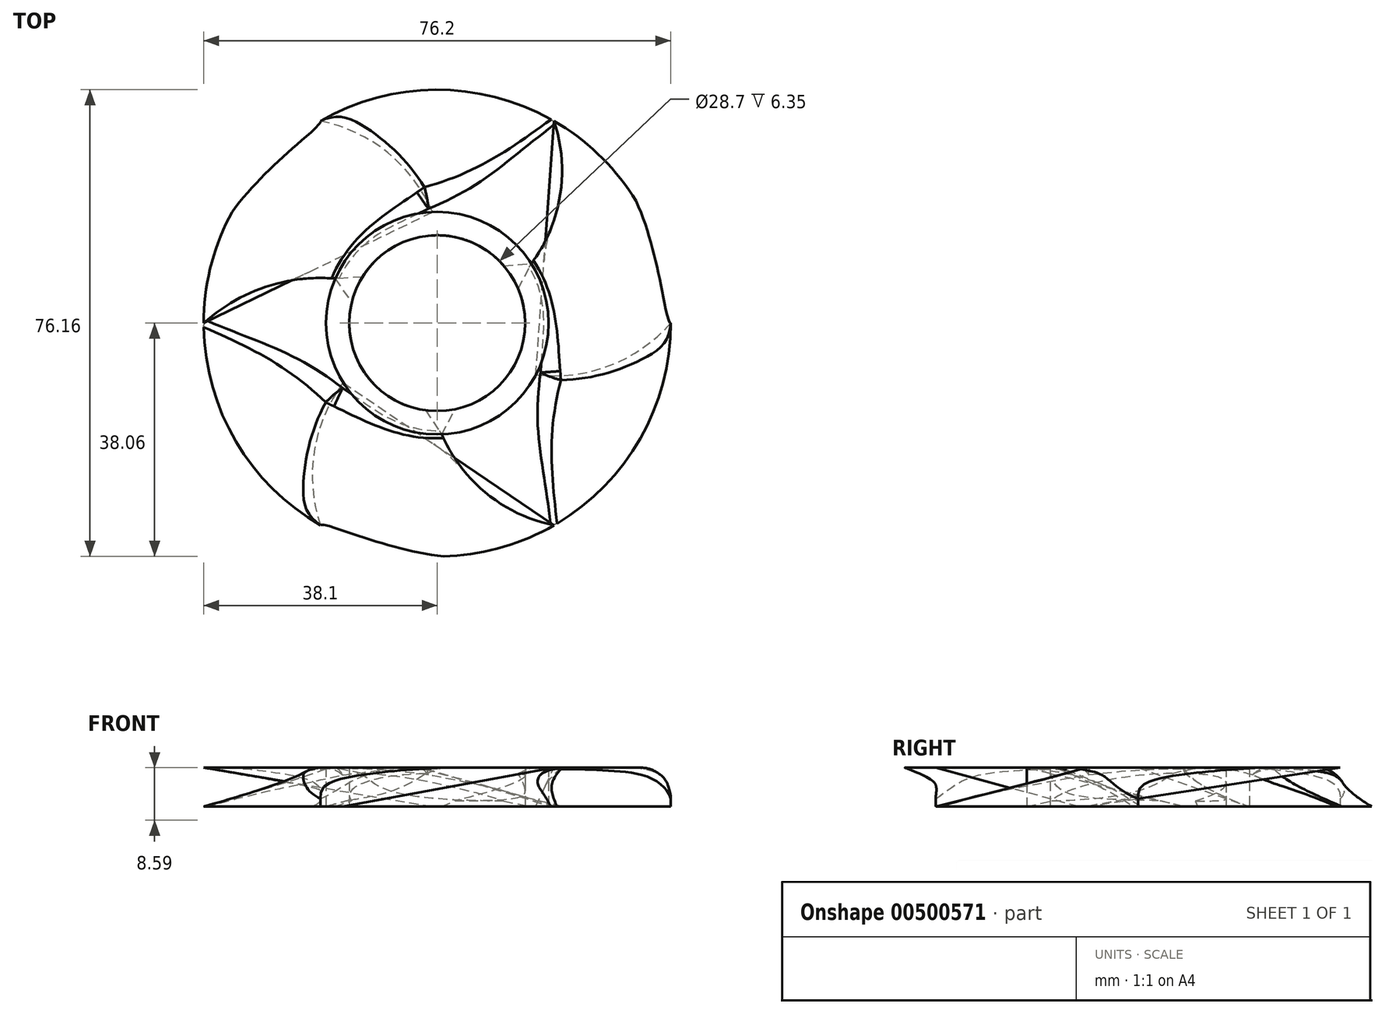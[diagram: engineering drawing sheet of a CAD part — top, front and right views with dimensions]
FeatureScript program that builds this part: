
annotation { "Feature Type Name" : "Feature", "Feature Type Description" : "" }
export const myFeature = defineFeature(function(context is Context, id is Id, definition is map)
    precondition{}
    {
        {
            var Q0;
            Q0=qCreatedBy(makeId("Top.planeOp"),FACE);
            var sketch = newSketch(context, id + "F0", { "sketchPlane" : qUnion([Q0])});
            skCircle(sketch, "E0", {"center": v(0, 0) * mm, "radius": 18.16 * mm});
            skCircle(sketch, "E1.cCircle", {"center": v(0, 0) * mm, "radius": 38.1 * mm, "construction": true});
            skPoint(sketch, "E1.0.midPoint", {"position": v(38.1, 0) * mm});
            skArc(sketch, "E2", {"start": v(15.34, 9.72) * mm, "mid": v(20.06, 20.9) * mm, "end": v(19.05, 33) * mm});
            skArc(sketch, "E3", {"start": v(16.09, -8.43) * mm, "mid": v(28.13, -6.92) * mm, "end": v(38.1, 0) * mm});
            skArc(sketch, "E4", {"start": v(0.75, -18.15) * mm, "mid": v(8.07, -27.82) * mm, "end": v(19.05, -33) * mm});
            skArc(sketch, "E5", {"start": v(-15.34, -9.72) * mm, "mid": v(-20.06, -20.9) * mm, "end": v(-19.05, -33) * mm});
            skArc(sketch, "E6", {"start": v(-16.64, 7.27) * mm, "mid": v(-28.13, 5.88) * mm, "end": v(-38.1, 0) * mm});
            skArc(sketch, "E7", {"start": v(-0.75, 18.15) * mm, "mid": v(-8.07, 27.82) * mm, "end": v(-19.05, 33) * mm});
            skCircle(sketch, "E8", {"center": v(0, 0) * mm, "radius": 38.1 * mm});
            skCircle(sketch, "E9", {"center": v(0, 0) * mm, "radius": 14.35 * mm});
            skSolve(sketch);
        }
        {
            var Q0;
            Q0=qCreatedBy(makeId("Top.planeOp"),FACE);
            cPlane(context, id + "F1", {"entities" : qUnion([Q0]), "cplaneType" : CPlaneType.OFFSET, "offset" : 6.35 * mm, "width" : 152.4 * mm, "height" : 152.4 * mm});
        }
        {
            var Q0;
            Q0=qCreatedBy(id+"F1.planeOp",FACE);
            var sketch = newSketch(context, id + "F2", { "sketchPlane" : qUnion([Q0])});
            skCircle(sketch, "E10", {"center": v(0, 0) * mm, "radius": 18.16 * mm});
            skCircle(sketch, "E11.cCircle", {"center": v(0, 0) * mm, "radius": 38.1 * mm, "construction": true});
            skPoint(sketch, "E11.0.midPoint", {"position": v(38.1, 0) * mm});
            skArc(sketch, "E12", {"start": v(15.34, 9.72) * mm, "mid": v(20.06, 20.9) * mm, "end": v(19.05, 33) * mm});
            skArc(sketch, "E13", {"start": v(16.09, -8.43) * mm, "mid": v(28.13, -6.92) * mm, "end": v(38.1, 0) * mm});
            skArc(sketch, "E14", {"start": v(0.75, -18.15) * mm, "mid": v(8.07, -27.82) * mm, "end": v(19.05, -33) * mm});
            skArc(sketch, "E15", {"start": v(-15.34, -9.72) * mm, "mid": v(-20.06, -20.9) * mm, "end": v(-19.05, -33) * mm});
            skArc(sketch, "E16", {"start": v(-16.64, 7.27) * mm, "mid": v(-28.13, 5.88) * mm, "end": v(-38.1, 0) * mm});
            skArc(sketch, "E17", {"start": v(-0.75, 18.15) * mm, "mid": v(-8.07, 27.82) * mm, "end": v(-19.05, 33) * mm});
            skCircle(sketch, "E18", {"center": v(0, 0) * mm, "radius": 38.1 * mm});
            skCircle(sketch, "E19", {"center": v(0, 0) * mm, "radius": 14.35 * mm});
            skSolve(sketch);
        }
        {
            var Q0;
            {var subQ0=sQuery(id+"F0.wireOp",EDGE,"E5");Q0=makeQuery(id+"F0.imprint","IMPRINT",FACE,{"disambiguationData":[TD([[makeQuery(id+"F0.imprint","IMPRINT",EDGE,{"derivedFrom":subQ0}),-1.0]])]});}
            var Q1;
            {var subQ0=sQuery(id+"F2.wireOp",EDGE,"E14");Q1=makeQuery(id+"F2.imprint","IMPRINT",FACE,{"disambiguationData":[TD([[makeQuery(id+"F2.imprint","IMPRINT",EDGE,{"derivedFrom":subQ0}),-1.0]])]});}
            loft(context, id + "F3", {"sheetProfilesArray" : [{ "sheetProfileEntities" : qUnion([Q0]) }, { "sheetProfileEntities" : qUnion([Q1]) }]});
        }
        {
            var Q0;
            {var subQ0=sQuery(id+"F0.wireOp",EDGE,"E3");Q0=makeQuery(id+"F0.imprint","IMPRINT",FACE,{"disambiguationData":[TD([[makeQuery(id+"F0.imprint","IMPRINT",EDGE,{"derivedFrom":subQ0}),-1.0]])]});}
            var Q1;
            {var subQ0=sQuery(id+"F2.wireOp",EDGE,"E12");Q1=makeQuery(id+"F2.imprint","IMPRINT",FACE,{"disambiguationData":[TD([[makeQuery(id+"F2.imprint","IMPRINT",EDGE,{"derivedFrom":subQ0}),-1.0]])]});}
            loft(context, id + "F4", {"sheetProfilesArray" : [{ "sheetProfileEntities" : qUnion([Q0]) }, { "sheetProfileEntities" : qUnion([Q1]) }]});
        }
        {
            var Q0;
            {var subQ0=sQuery(id+"F2.wireOp",EDGE,"E16");Q0=makeQuery(id+"F2.imprint","IMPRINT",FACE,{"disambiguationData":[TD([[makeQuery(id+"F2.imprint","IMPRINT",EDGE,{"derivedFrom":subQ0}),-1.0]])]});}
            var Q1;
            {var subQ0=sQuery(id+"F0.wireOp",EDGE,"E2");Q1=makeQuery(id+"F0.imprint","IMPRINT",FACE,{"disambiguationData":[TD([[makeQuery(id+"F0.imprint","IMPRINT",EDGE,{"derivedFrom":subQ0}),1.0]])]});}
            loft(context, id + "F5", {"sheetProfilesArray" : [{ "sheetProfileEntities" : qUnion([Q0]) }, { "sheetProfileEntities" : qUnion([Q1]) }]});
        }
        {
            var Q0;
            Q0=makeQuery(id+"F5.opLoft","MID_CAP_EDGE",EDGE,{"disambiguationData":[OSD([sQuery(id+"F2.wireOp",EDGE,"E10"),sQuery(id+"F2.wireOp",EDGE,"E17"),sQuery(id+"F2.wireOp",EDGE,"E18")])],"capPos":0.0});
            fillet(context, id + "F6", {"entities" : qUnion([Q0]), "radius" : 5.08 * mm, "tangentPropagation" : true, "allowEdgeOverflow" : false});
        }
        {
            var Q0;
            Q0=makeQuery(id+"F4.opLoft","MID_CAP_EDGE",EDGE,{"disambiguationData":[OSD([sQuery(id+"F2.wireOp",EDGE,"E10"),sQuery(id+"F2.wireOp",EDGE,"E13"),sQuery(id+"F2.wireOp",EDGE,"E18")])],"capPos":1.0});
            fillet(context, id + "F7", {"entities" : qUnion([Q0]), "radius" : 5.08 * mm, "tangentPropagation" : true, "allowEdgeOverflow" : false});
        }
        {
            var Q0;
            Q0=makeQuery(id+"F3.opLoft","MID_CAP_EDGE",EDGE,{"disambiguationData":[OSD([sQuery(id+"F2.wireOp",EDGE,"E10"),sQuery(id+"F2.wireOp",EDGE,"E15"),sQuery(id+"F2.wireOp",EDGE,"E18")])],"capPos":1.0});
            fillet(context, id + "F8", {"entities" : qUnion([Q0]), "radius" : 5.08 * mm, "tangentPropagation" : true, "allowEdgeOverflow" : false});
        }
        {
            var Q0;
            Q0=makeQuery(id+"F3.opLoft","SWEPT_EDGE",EDGE,{"disambiguationData":[OSD([sQuery(id+"F0.wireOp",EDGE,"E6"),sQuery(id+"F0.wireOp",EDGE,"E8"),sQuery(id+"F2.wireOp",EDGE,"E10"),sQuery(id+"F2.wireOp",EDGE,"E15")])]});
            fillet(context, id + "F9", {"entities" : qUnion([Q0]), "radius" : 5.08 * mm, "tangentPropagation" : true, "allowEdgeOverflow" : false});
        }
        {
            var Q0;
            Q0=makeQuery(id+"F5.opLoft","SWEPT_EDGE",EDGE,{"disambiguationData":[OSD([sQuery(id+"F0.wireOp",EDGE,"E2"),sQuery(id+"F0.wireOp",EDGE,"E8"),sQuery(id+"F2.wireOp",EDGE,"E10"),sQuery(id+"F2.wireOp",EDGE,"E17")])]});
            fillet(context, id + "F10", {"entities" : qUnion([Q0]), "radius" : 5.08 * mm, "tangentPropagation" : true, "allowEdgeOverflow" : false});
        }
        {
            var Q0;
            Q0=makeQuery(id+"F4.opLoft","SWEPT_EDGE",EDGE,{"disambiguationData":[OSD([sQuery(id+"F0.wireOp",EDGE,"E4"),sQuery(id+"F0.wireOp",EDGE,"E8"),sQuery(id+"F2.wireOp",EDGE,"E10"),sQuery(id+"F2.wireOp",EDGE,"E13")])]});
            fillet(context, id + "F11", {"entities" : qUnion([Q0]), "radius" : 5.08 * mm, "tangentPropagation" : true, "allowEdgeOverflow" : false});
        }
        {
            var Q0;
            Q0=makeQuery(id+"F0.imprint","IMPRINT",FACE,{"disambiguationData":[TD([[makeQuery(id+"F0.imprint","IMPRINT",EDGE,{"derivedFrom":sQuery(id+"F0.wireOp",EDGE,"E9")}),-1.0]])]});
            extrude(context, id + "F12", {"entities" : qUnion([Q0]), "depth" : 6.35 * mm, "offsetDistance" : 25.4 * mm});
        }
        {
            var Q0;
            Q0=makeQuery(id+"F0.imprint","IMPRINT",FACE,{"disambiguationData":[TD([[makeQuery(id+"F0.imprint","IMPRINT",EDGE,{"derivedFrom":sQuery(id+"F0.wireOp",EDGE,"E9")}),1.0]])]});
            extrude(context, id + "F13", {"entities" : qUnion([Q0]), "operationType" : NewBodyOperationType.REMOVE, "depth" : 6.35 * mm, "offsetDistance" : 25.4 * mm});
        }
    });
